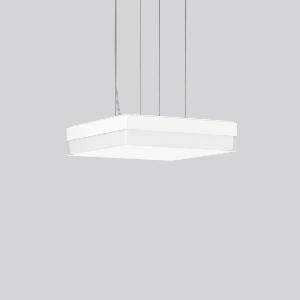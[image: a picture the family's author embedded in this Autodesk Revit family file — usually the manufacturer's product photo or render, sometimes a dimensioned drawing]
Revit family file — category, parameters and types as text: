
# Revit family: flat_slim_square_312542_002_5d0e
name_source: partatom
category: Lighting Fixtures
units: mm (PartAtom-declared; Revit-internal decimal feet)

## family parameters
Cut with Voids When Loaded = No
Host = Face
Light Source = No
Part Type = Normal
Room Calculation Point = No
Round Connector Dimension = Use Diameter
Shared = No

## types (1)
- MultiLumen 2 840 (1 x LED Modul 840, 2200 lm, 4000)
    Apparent Load = 19 VA
    CIE Flux Codes = 43 75 93 91 100
    Color Rendering = 80
    Color Temperature = 4000
    Default Elevation = 1800 mm
    Height = 70 mm
    Lamp = 1 x LED Modul 840
    Lamp Light Flux = 2200 lm
    Lamp count = 1
    Length = 300 mm
    Lifetime = 50000 h
    Luminous efficacy = 116 lm/W
    Manufacturer = RZB
    ModVariant = No
    Model = 312542.002
    Mounting Place = Ceiling
    Mounting Type = Pendant
    Number of Poles = 1
    OnlyDefault = Yes
    Power Factor = 1
    Product Name = FLAT SLIM square
    Product group = Pendant luminaires
    ProductGroupID = 902
    Protection Class = Protection class I
    Protection Degree = IP 40
    RLX_Detail_Level = 1
    RLX_Emergency_Light_Flux = 0 lm
    RLX_Emergency_Type = 0
    RLX_Emergency_Type_DB = No
    RlxData = <blob elided: 13657 chars, md5=03b53235>
    Socket = socket
    Standby Power = 0 W
    System Light Flux = 2200 lm
    System Power = 19 W
    Type Comments = MultiLumen 2 840
    Type Image = 312542.002.jpg
    URL = http://relux.com
    VarID = multilumen_2_840
    Voltage = 230 V
    Voltage Range = 220-240 V
    Weight = 0.00 kg
    Width = 300 mm

## geometry (parser evidence)
native form markers: Sweep x14
no freeform markers — native parametric forms only
